# Revit family: Layout-Teknion-Zones_Ledge_Table_01-R2015
name_source: partatom
category: Furniture Systems
revit_build: Autodesk Revit Architecture 2015 (Build: 20140323_1530(x64)
units: mm (PartAtom-declared; Revit-internal decimal feet)

## types (1)
- Canteen Tables 01
    Apparent Load = 0 VA
    Apparent Load Note = Complete With Canteen Table Type Information
    Assembly Code = E2020200
    Connector Description = Without Power Connector
    Depth = 6' - 4"
    Description = 5'-0" x 11'-0"
    Height = 3' - 6 15/16"
    Manufacturer = Teknion
    Manufacturer Fax = 416.661.4586
    Model = Ledge Table 01
    Product Line = Zones
    Product Page URL = http://teknionplanningtool.com
    Series = Zones
    Sustainability Data = http://www.teknion.com
    URL = www.teknion.com
    Unit Weight URL = http://www.teknion.com
    Voltage = 0 V
    Voltage Note = Complete With Canteen Table Type Information
    Warranty = http://www.teknion.com
    Width = 10' - 3"

## geometry (parser evidence)
native form markers: Blend x112, Sweep x33
no freeform markers — native parametric forms only
